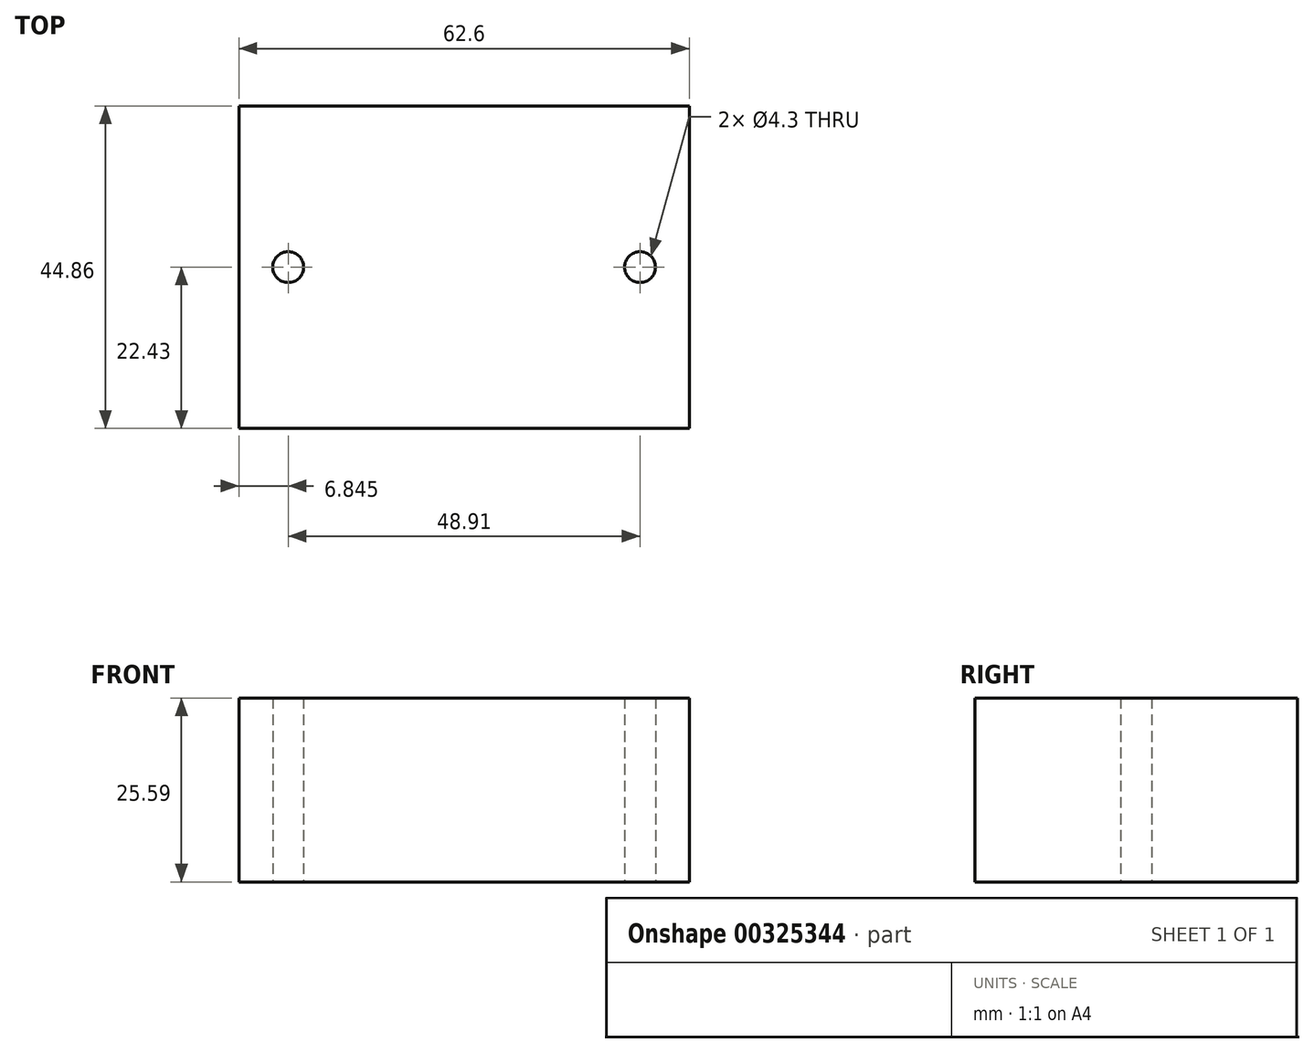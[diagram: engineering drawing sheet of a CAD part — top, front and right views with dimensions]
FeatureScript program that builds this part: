
annotation { "Feature Type Name" : "Feature", "Feature Type Description" : "" }
export const myFeature = defineFeature(function(context is Context, id is Id, definition is map)
    precondition{}
    {
        {
            var Q0;
            Q0=qCreatedBy(makeId("Top.planeOp"),FACE);
            var sketch = newSketch(context, id + "F0", { "sketchPlane" : qUnion([Q0])});
            skLineSegment(sketch, "E0.bottom", {"start": v(31.3, -22.43) * mm, "end": v(-31.3, -22.43) * mm});
            skLineSegment(sketch, "E0.top", {"start": v(31.3, 22.43) * mm, "end": v(-31.3, 22.43) * mm});
            skLineSegment(sketch, "E0.left", {"start": v(31.3, -22.43) * mm, "end": v(31.3, 22.43) * mm});
            skLineSegment(sketch, "E0.right", {"start": v(-31.3, -22.43) * mm, "end": v(-31.3, 22.43) * mm});
            skPoint(sketch, "E0.middle", {"position": v(0, 0) * mm});
            skCircle(sketch, "E1", {"center": v(-24.45, 0) * mm, "radius": 2.15 * mm});
            skCircle(sketch, "E2", {"center": v(24.45, 0) * mm, "radius": 2.15 * mm});
            skSolve(sketch);
        }
        {
            var Q0;
            Q0 = qSketchRegion(id + "F0", true);
            extrude(context, id + "F1", {"entities" : qUnion([Q0]), "depth" : 25.59 * mm});
        }
    });
